# Revit family: 3461A_NX_Dry_Contact_Interface_Module
name_source: partatom
category: Communication Devices
units: mm (PartAtom-declared; Revit-internal decimal feet)

## family parameters
Cut with Voids When Loaded = No
Host = Face
Maintain Annotation Orientation = No
OmniClass Number = 23.85.80.11.27
OmniClass Title = Lighting Controls
Part Type = Normal
Room Calculation Point = No
Round Connector Dimension = Use Diameter
Shared = Yes

## types (1)
- 3461A_NX_Dry_Contact_Interface_Module
    Apparent Load = 0 VA
    Assembly Code = D5090
    Black Material = Paint -  Black Matte Textured
    Default Elevation = 48 "
    Description = It provides a simple way to incorporate standard dry contact inputs and outputs into the NX control
    Features = Programmable from the NX Area Controller
• Six dry contact inputs with pilots
• Accommodates 2 and 3 wire inputs (momentary or maintained)
• Six Form-C dry contact outputs
• Removable terminal blocks for easy connections
• DIN rail mounting in the NX Accessory Enclosure
• Requires the NX Device Network Interface Module for connection to
    Green Element = Plastic -  Green
    Manufacturer = NX Lighting Controls
    Model = NX Dry Contact Module
    Steel = Metal-Galvanized_Steel
    Type Comments = NX Dry Contact Module
    URL = https://www.currentlighting.com
    Voltage = 24 V
    Warranty = 5-Years Warranty
    White Element = Glass, White, High Luminance

## geometry (parser evidence)
native form markers: Sweep x2
no freeform markers — native parametric forms only
